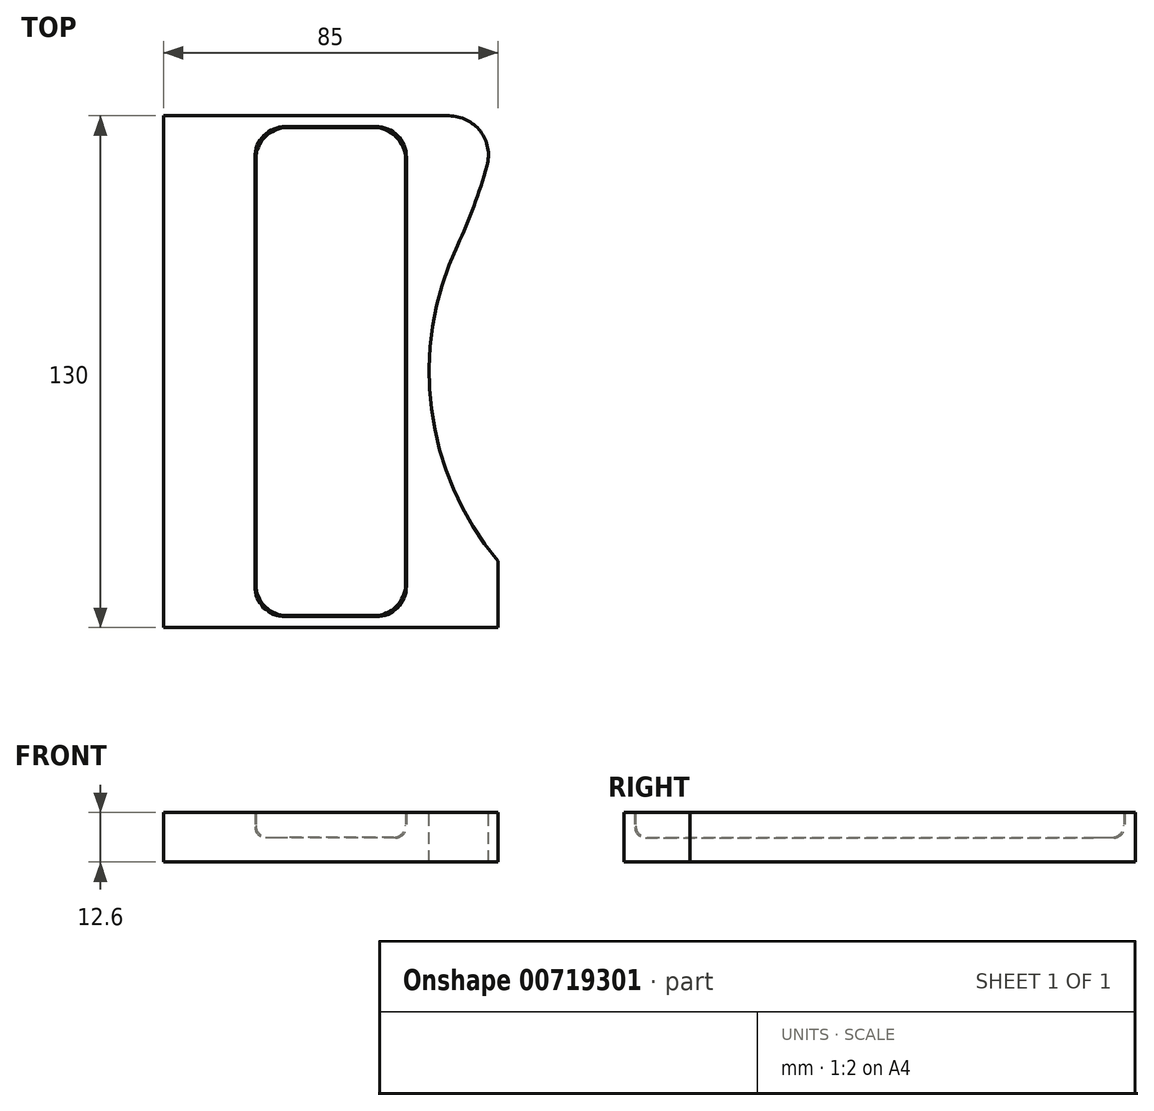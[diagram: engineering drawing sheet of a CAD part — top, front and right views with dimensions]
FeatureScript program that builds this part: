
annotation { "Feature Type Name" : "Feature", "Feature Type Description" : "" }
export const myFeature = defineFeature(function(context is Context, id is Id, definition is map)
    precondition{}
    {
        {
            var Q0;
            Q0=qCreatedBy(makeId("Top.planeOp"),FACE);
            var sketch = newSketch(context, id + "F0", { "sketchPlane" : qUnion([Q0])});
            skLineSegment(sketch, "E0.bottom", {"start": v(19, -62) * mm, "end": v(-19, -62) * mm});
            skLineSegment(sketch, "E0.top", {"start": v(19, 62) * mm, "end": v(-19, 62) * mm});
            skLineSegment(sketch, "E0.left", {"start": v(19, -62) * mm, "end": v(19, 62) * mm});
            skLineSegment(sketch, "E0.right", {"start": v(-19, -62) * mm, "end": v(-19, 62) * mm});
            skPoint(sketch, "E0.middle", {"position": v(0, 0) * mm});
            skSolve(sketch);
        }
        {
            var Q0;
            Q0=makeQuery(id+"F0.imprint","IMPRINT",FACE,{"disambiguationData":[TD([[makeQuery(id+"F0.imprint","IMPRINT",EDGE,{"derivedFrom":sQuery(id+"F0.wireOp",EDGE,"E0.bottom")}),-1.0]])]});
            extrude(context, id + "F1", {"entities" : qUnion([Q0]), "depth" : 6.3 * mm, "offsetDistance" : 25 * mm});
        }
        {
            var Q0;
            Q0=makeQuery(id+"F1.opExtrude","SWEPT_EDGE",EDGE,{"disambiguationData":[OSD([sQuery(id+"F0.wireOp",EDGE,"E0.top"),sQuery(id+"F0.wireOp",EDGE,"E0.left")])]});
            var Q1;
            Q1=makeQuery(id+"F1.opExtrude","SWEPT_EDGE",EDGE,{"disambiguationData":[OSD([sQuery(id+"F0.wireOp",EDGE,"E0.top"),sQuery(id+"F0.wireOp",EDGE,"E0.right")])]});
            var Q2;
            Q2=makeQuery(id+"F1.opExtrude","SWEPT_EDGE",EDGE,{"disambiguationData":[OSD([sQuery(id+"F0.wireOp",EDGE,"E0.bottom"),sQuery(id+"F0.wireOp",EDGE,"E0.left")])]});
            var Q3;
            Q3=makeQuery(id+"F1.opExtrude","SWEPT_EDGE",EDGE,{"disambiguationData":[OSD([sQuery(id+"F0.wireOp",EDGE,"E0.bottom"),sQuery(id+"F0.wireOp",EDGE,"E0.right")])]});
            fillet(context, id + "F2", {"entities" : qUnion([Q0, Q1, Q2, Q3]), "radius" : 8 * mm, "tangentPropagation" : true, "allowEdgeOverflow" : false});
        }
        {
            var Q0;
            Q0=makeQuery(id+"F1.opExtrude","CAP_FACE",FACE,{"disambiguationData":[OSD([sQuery(id+"F0.wireOp",EDGE,"E0.bottom"),sQuery(id+"F0.wireOp",EDGE,"E0.top"),sQuery(id+"F0.wireOp",EDGE,"E0.left"),sQuery(id+"F0.wireOp",EDGE,"E0.right")])],"isStart":true});
            fillet(context, id + "F3", {"entities" : qUnion([Q0]), "radius" : 3 * mm, "tangentPropagation" : true, "allowEdgeOverflow" : false});
        }
        {
            var Q0;
            Q0=qCreatedBy(makeId("Top.planeOp"),FACE);
            var sketch = newSketch(context, id + "F4", { "sketchPlane" : qUnion([Q0])});
            skLineSegment(sketch, "E1.bottom", {"start": v(19.25, -62.25) * mm, "end": v(-19.25, -62.25) * mm});
            skLineSegment(sketch, "E1.top", {"start": v(19.25, 62.25) * mm, "end": v(-19.25, 62.25) * mm});
            skLineSegment(sketch, "E1.left", {"start": v(19.25, -62.25) * mm, "end": v(19.25, 62.25) * mm});
            skLineSegment(sketch, "E1.right", {"start": v(-19.25, -62.25) * mm, "end": v(-19.25, 62.25) * mm});
            skPoint(sketch, "E1.middle", {"position": v(0, 0) * mm});
            skLineSegment(sketch, "E2.bottom", {"start": v(42.5, -65) * mm, "end": v(-42.5, -65) * mm});
            skLineSegment(sketch, "E2.top", {"start": v(42.5, 65) * mm, "end": v(-42.5, 65) * mm});
            skLineSegment(sketch, "E2.left", {"start": v(42.5, -65) * mm, "end": v(42.5, 65) * mm});
            skLineSegment(sketch, "E2.right", {"start": v(-42.5, -65) * mm, "end": v(-42.5, 65) * mm});
            skCircle(sketch, "E3", {"center": v(0, 65) * mm, "radius": 42.5 * mm});
            skCircle(sketch, "E4", {"center": v(0, -65) * mm, "radius": 42.5 * mm});
            skSolve(sketch);
        }
        {
            var Q0;
            Q0=makeQuery(id+"F4.imprint","IMPRINT",FACE,{"disambiguationData":[TD([[makeQuery(id+"F4.imprint","IMPRINT",EDGE,{"derivedFrom":sQuery(id+"F4.wireOp",EDGE,"E1.bottom")}),1.0]])]});
            var Q1;
            {var subQ5=sQuery(id+"F4.wireOp",EDGE,"E2.right");Q1=makeQuery(id+"F4.imprint","IMPRINT",FACE,{"disambiguationData":[TD([[makeQuery(id+"F4.imprint","IMPRINT",EDGE,{"derivedFrom":subQ5}),-1.0]])]});}
            var Q2;
            {var subQ5=sQuery(id+"F4.wireOp",EDGE,"E2.left");Q2=makeQuery(id+"F4.imprint","IMPRINT",FACE,{"disambiguationData":[TD([[makeQuery(id+"F4.imprint","IMPRINT",EDGE,{"derivedFrom":subQ5}),1.0]])]});}
            var Q3;
            {var subQ1=sQuery(id+"F4.wireOp",EDGE,"E1.top");Q3=makeQuery(id+"F4.imprint","IMPRINT",FACE,{"disambiguationData":[TD([[makeQuery(id+"F4.imprint","IMPRINT",EDGE,{"derivedFrom":subQ1}),-1.0]])]});}
            extrude(context, id + "F5", {"entities" : qUnion([Q0, Q1, Q2, Q3]), "endBound" : BoundingType.SYMMETRIC, "depth" : 12.6 * mm, "offsetDistance" : 25 * mm});
        }
        {
            var Q0;
            Q0=makeQuery(id+"F5.opExtrude","CAP_FACE",FACE,{"disambiguationData":[OSD([sQuery(id+"F4.wireOp",EDGE,"E1.bottom"),sQuery(id+"F4.wireOp",EDGE,"E1.top"),sQuery(id+"F4.wireOp",EDGE,"E1.left"),sQuery(id+"F4.wireOp",EDGE,"E1.right"),sQuery(id+"F4.wireOp",EDGE,"E2.bottom"),sQuery(id+"F4.wireOp",EDGE,"E2.top"),sQuery(id+"F4.wireOp",EDGE,"E2.left"),sQuery(id+"F4.wireOp",EDGE,"E2.right")])],"isStart":true});
            var sketch = newSketch(context, id + "F6", { "sketchPlane" : qUnion([Q0])});
            skLineSegment(sketch, "E5.bottom", {"start": v(19.25, -62.25) * mm, "end": v(-19.25, -62.25) * mm});
            skLineSegment(sketch, "E5.top", {"start": v(19.25, 62.25) * mm, "end": v(-19.25, 62.25) * mm});
            skLineSegment(sketch, "E5.left", {"start": v(19.25, -62.25) * mm, "end": v(19.25, 62.25) * mm});
            skLineSegment(sketch, "E5.right", {"start": v(-19.25, -62.25) * mm, "end": v(-19.25, 62.25) * mm});
            skPoint(sketch, "E5.middle", {"position": v(0, 0) * mm});
            skSolve(sketch);
        }
        {
            var Q0;
            Q0=makeQuery(id+"F6.imprint","IMPRINT",FACE,{"disambiguationData":[TD([[makeQuery(id+"F6.imprint","IMPRINT",EDGE,{"derivedFrom":sQuery(id+"F6.wireOp",EDGE,"E5.bottom")}),-1.0]])]});
            extrude(context, id + "F7", {"entities" : qUnion([Q0]), "operationType" : NewBodyOperationType.ADD, "oppositeDirection" : true, "depth" : 6.15 * mm, "offsetDistance" : 25 * mm});
        }
        {
            var Q0;
            Q0=makeQuery(id+"F5.opExtrude","SWEPT_EDGE",EDGE,{"disambiguationData":[OSD([sQuery(id+"F4.wireOp",EDGE,"E1.bottom"),sQuery(id+"F4.wireOp",EDGE,"E1.left")])]});
            var Q1;
            Q1=makeQuery(id+"F5.opExtrude","SWEPT_EDGE",EDGE,{"disambiguationData":[OSD([sQuery(id+"F4.wireOp",EDGE,"E1.bottom"),sQuery(id+"F4.wireOp",EDGE,"E1.right")])]});
            var Q2;
            Q2=makeQuery(id+"F5.opExtrude","SWEPT_EDGE",EDGE,{"disambiguationData":[OSD([sQuery(id+"F4.wireOp",EDGE,"E1.top"),sQuery(id+"F4.wireOp",EDGE,"E1.left")])]});
            var Q3;
            Q3=makeQuery(id+"F5.opExtrude","SWEPT_EDGE",EDGE,{"disambiguationData":[OSD([sQuery(id+"F4.wireOp",EDGE,"E1.top"),sQuery(id+"F4.wireOp",EDGE,"E1.right")])]});
            fillet(context, id + "F8", {"entities" : qUnion([Q0, Q1, Q2, Q3]), "radius" : 7.75 * mm, "tangentPropagation" : true, "allowEdgeOverflow" : false});
        }
        {
            var Q0;
            Q0=makeQuery(id+"F7.opExtrude","CAP_FACE",FACE,{"disambiguationData":[OSD([sQuery(id+"F6.wireOp",EDGE,"E5.bottom"),sQuery(id+"F6.wireOp",EDGE,"E5.top"),sQuery(id+"F6.wireOp",EDGE,"E5.left"),sQuery(id+"F6.wireOp",EDGE,"E5.right")])],"isStart":false});
            fillet(context, id + "F9", {"entities" : qUnion([Q0]), "radius" : 2.75 * mm, "tangentPropagation" : true, "allowEdgeOverflow" : false});
        }
        {
            var Q0;
            Q0=makeQuery(id+"F5.opExtrude","CAP_FACE",FACE,{"disambiguationData":[OSD([sQuery(id+"F4.wireOp",EDGE,"E1.bottom"),sQuery(id+"F4.wireOp",EDGE,"E1.top"),sQuery(id+"F4.wireOp",EDGE,"E1.left"),sQuery(id+"F4.wireOp",EDGE,"E1.right"),sQuery(id+"F4.wireOp",EDGE,"E2.bottom"),sQuery(id+"F4.wireOp",EDGE,"E2.top"),sQuery(id+"F4.wireOp",EDGE,"E2.left"),sQuery(id+"F4.wireOp",EDGE,"E2.right")])],"isStart":false});
            var sketch = newSketch(context, id + "F10", { "sketchPlane" : qUnion([Q0])});
            skLineSegment(sketch, "E6", {"start": v(-75.4, 0) * mm, "end": v(78.09, 0) * mm, "construction": true});
            skPoint(sketch, "E6.startSnap0", {"position": v(-42.5, 0) * mm});
            skPoint(sketch, "E7.endSnap0", {"position": v(0, -92.5) * mm});
            skLineSegment(sketch, "E8", {"start": v(0, -120.38) * mm, "end": v(0, 105.72) * mm, "construction": true});
            skCircle(sketch, "E9", {"center": v(100, 0) * mm, "radius": 75 * mm});
            skPoint(sketch, "E10", {"position": v(0, 0) * mm});
            skCircle(sketch, "E11.MirrorC", {"center": v(-100, 0) * mm, "radius": 75 * mm});
            skSolve(sketch);
        }
        {
            var Q0;
            {var subQ0=sQuery(id+"F10.wireOp",EDGE,"E11.MirrorC");var subQ1=makeQuery(id+"F5.opExtrude","CAP_EDGE",EDGE,{"disambiguationData":[OSD([sQuery(id+"F4.wireOp",EDGE,"E2.right")])],"isStart":false});var subQ2=makeQuery(id+"F10.imprint","INTERSECT",VERTEX,{"disambiguationData":[OD(0.0)],"derivedFrom":[subQ1,subQ0]});Q0=makeQuery(id+"F10.imprint","IMPRINT",FACE,{"disambiguationData":[TD([[makeQuery(id+"F10.imprint","IMPRINT",EDGE,{"disambiguationData":[TD([[subQ2,1.0]])],"derivedFrom":subQ0}),-1.0]])]});}
            var Q1;
            {var subQ0=sQuery(id+"F10.wireOp",EDGE,"E9");var subQ1=makeQuery(id+"F5.opExtrude","CAP_EDGE",EDGE,{"disambiguationData":[OSD([sQuery(id+"F4.wireOp",EDGE,"E2.left")])],"isStart":false});var subQ2=makeQuery(id+"F10.imprint","INTERSECT",VERTEX,{"disambiguationData":[OD(0.0)],"derivedFrom":[subQ1,subQ0]});Q1=makeQuery(id+"F10.imprint","IMPRINT",FACE,{"disambiguationData":[TD([[makeQuery(id+"F10.imprint","IMPRINT",EDGE,{"disambiguationData":[TD([[subQ2,1.0]])],"derivedFrom":subQ0}),1.0]])]});}
            extrude(context, id + "F11", {"entities" : qUnion([Q0, Q1]), "operationType" : NewBodyOperationType.REMOVE, "endBound" : BoundingType.THROUGH_ALL, "oppositeDirection" : true, "depth" : 25 * mm, "offsetDistance" : 25 * mm});
        }
        {
            var Q0;
            {var subQ0=sQuery(id+"F10.wireOp",EDGE,"E9");var subQ1=sQuery(id+"F4.wireOp",EDGE,"E2.left");Q0=makeQuery(id+"F11.boolean.opBoolean","COPY",EDGE,{"derivedFrom":makeQuery(id+"F11.opExtrude","SWEPT_EDGE",EDGE,{"disambiguationData":[OSD([subQ1,subQ0]),TDD([makeQuery(id+"F10.imprint","INTERSECT",VERTEX,{"disambiguationData":[OD(0.0)],"derivedFrom":[makeQuery(id+"F5.opExtrude","CAP_EDGE",EDGE,{"disambiguationData":[OSD([subQ1])],"isStart":false}),subQ0]})])]})});}
            var Q1;
            {var subQ0=sQuery(id+"F10.wireOp",EDGE,"E9");var subQ1=sQuery(id+"F4.wireOp",EDGE,"E2.left");Q1=makeQuery(id+"F11.boolean.opBoolean","COPY",EDGE,{"derivedFrom":makeQuery(id+"F11.opExtrude","SWEPT_EDGE",EDGE,{"disambiguationData":[OSD([subQ1,subQ0]),TDD([makeQuery(id+"F10.imprint","INTERSECT",VERTEX,{"disambiguationData":[OD(1.0)],"derivedFrom":[makeQuery(id+"F5.opExtrude","CAP_EDGE",EDGE,{"disambiguationData":[OSD([subQ1])],"isStart":false}),subQ0]})])]})});}
            var Q2;
            {var subQ0=sQuery(id+"F10.wireOp",EDGE,"E11.MirrorC");var subQ1=sQuery(id+"F4.wireOp",EDGE,"E2.right");Q2=makeQuery(id+"F11.boolean.opBoolean","COPY",EDGE,{"derivedFrom":makeQuery(id+"F11.opExtrude","SWEPT_EDGE",EDGE,{"disambiguationData":[OSD([subQ1,subQ0]),TDD([makeQuery(id+"F10.imprint","INTERSECT",VERTEX,{"disambiguationData":[OD(0.0)],"derivedFrom":[makeQuery(id+"F5.opExtrude","CAP_EDGE",EDGE,{"disambiguationData":[OSD([subQ1])],"isStart":false}),subQ0]})])]})});}
            var Q3;
            {var subQ0=sQuery(id+"F10.wireOp",EDGE,"E11.MirrorC");var subQ1=sQuery(id+"F4.wireOp",EDGE,"E2.right");Q3=makeQuery(id+"F11.boolean.opBoolean","COPY",EDGE,{"derivedFrom":makeQuery(id+"F11.opExtrude","SWEPT_EDGE",EDGE,{"disambiguationData":[OSD([subQ1,subQ0]),TDD([makeQuery(id+"F10.imprint","INTERSECT",VERTEX,{"disambiguationData":[OD(1.0)],"derivedFrom":[makeQuery(id+"F5.opExtrude","CAP_EDGE",EDGE,{"disambiguationData":[OSD([subQ1])],"isStart":false}),subQ0]})])]})});}
            fillet(context, id + "F12", {"entities" : qUnion([Q0, Q1, Q2, Q3]), "radius" : 125 * mm, "tangentPropagation" : true, "allowEdgeOverflow" : false});
        }
        {
            var Q0;
            {var subQ0=sQuery(id+"F10.wireOp",EDGE,"E11.MirrorC");var subQ1=sQuery(id+"F4.wireOp",EDGE,"E2.right");Q0=makeQuery(id+"F12.opFillet","BLEND_EDGE",EDGE,{"blendedFrom":[makeQuery(id+"F11.boolean.opBoolean","COPY",EDGE,{"derivedFrom":makeQuery(id+"F11.opExtrude","SWEPT_EDGE",EDGE,{"disambiguationData":[OSD([subQ1,subQ0]),TDD([makeQuery(id+"F10.imprint","INTERSECT",VERTEX,{"disambiguationData":[OD(1.0)],"derivedFrom":[makeQuery(id+"F5.opExtrude","CAP_EDGE",EDGE,{"disambiguationData":[OSD([subQ1])],"isStart":false}),subQ0]})])]})}),makeQuery(id+"F5.opExtrude","SWEPT_FACE",FACE,{"disambiguationData":[OSD([sQuery(id+"F4.wireOp",EDGE,"E2.top")])]})],"blendedInto":[makeQuery(id+"F5.opExtrude","SWEPT_FACE",FACE,{"disambiguationData":[OSD([sQuery(id+"F4.wireOp",EDGE,"E2.top")])]})]});}
            var Q1;
            {var subQ0=sQuery(id+"F10.wireOp",EDGE,"E9");var subQ1=sQuery(id+"F4.wireOp",EDGE,"E2.left");Q1=makeQuery(id+"F12.opFillet","BLEND_EDGE",EDGE,{"blendedFrom":[makeQuery(id+"F11.boolean.opBoolean","COPY",EDGE,{"derivedFrom":makeQuery(id+"F11.opExtrude","SWEPT_EDGE",EDGE,{"disambiguationData":[OSD([subQ1,subQ0]),TDD([makeQuery(id+"F10.imprint","INTERSECT",VERTEX,{"disambiguationData":[OD(1.0)],"derivedFrom":[makeQuery(id+"F5.opExtrude","CAP_EDGE",EDGE,{"disambiguationData":[OSD([subQ1])],"isStart":false}),subQ0]})])]})}),makeQuery(id+"F5.opExtrude","SWEPT_FACE",FACE,{"disambiguationData":[OSD([sQuery(id+"F4.wireOp",EDGE,"E2.top")])]})],"blendedInto":[makeQuery(id+"F5.opExtrude","SWEPT_FACE",FACE,{"disambiguationData":[OSD([sQuery(id+"F4.wireOp",EDGE,"E2.top")])]})]});}
            var Q2;
            {var subQ0=sQuery(id+"F10.wireOp",EDGE,"E11.MirrorC");var subQ1=sQuery(id+"F4.wireOp",EDGE,"E2.right");Q2=makeQuery(id+"F12.opFillet","BLEND_EDGE",EDGE,{"blendedFrom":[makeQuery(id+"F11.boolean.opBoolean","COPY",EDGE,{"derivedFrom":makeQuery(id+"F11.opExtrude","SWEPT_EDGE",EDGE,{"disambiguationData":[OSD([subQ1,subQ0]),TDD([makeQuery(id+"F10.imprint","INTERSECT",VERTEX,{"disambiguationData":[OD(0.0)],"derivedFrom":[makeQuery(id+"F5.opExtrude","CAP_EDGE",EDGE,{"disambiguationData":[OSD([subQ1])],"isStart":false}),subQ0]})])]})}),makeQuery(id+"F5.opExtrude","SWEPT_FACE",FACE,{"disambiguationData":[OSD([sQuery(id+"F4.wireOp",EDGE,"E2.bottom")])]})],"blendedInto":[makeQuery(id+"F5.opExtrude","SWEPT_FACE",FACE,{"disambiguationData":[OSD([sQuery(id+"F4.wireOp",EDGE,"E2.bottom")])]})]});}
            var Q3;
            {var subQ0=sQuery(id+"F10.wireOp",EDGE,"E9");var subQ1=sQuery(id+"F4.wireOp",EDGE,"E2.left");Q3=makeQuery(id+"F12.opFillet","BLEND_EDGE",EDGE,{"blendedFrom":[makeQuery(id+"F11.boolean.opBoolean","COPY",EDGE,{"derivedFrom":makeQuery(id+"F11.opExtrude","SWEPT_EDGE",EDGE,{"disambiguationData":[OSD([subQ1,subQ0]),TDD([makeQuery(id+"F10.imprint","INTERSECT",VERTEX,{"disambiguationData":[OD(0.0)],"derivedFrom":[makeQuery(id+"F5.opExtrude","CAP_EDGE",EDGE,{"disambiguationData":[OSD([subQ1])],"isStart":false}),subQ0]})])]})}),makeQuery(id+"F5.opExtrude","SWEPT_FACE",FACE,{"disambiguationData":[OSD([sQuery(id+"F4.wireOp",EDGE,"E2.bottom")])]})],"blendedInto":[makeQuery(id+"F5.opExtrude","SWEPT_FACE",FACE,{"disambiguationData":[OSD([sQuery(id+"F4.wireOp",EDGE,"E2.bottom")])]})]});}
            fillet(context, id + "F13", {"entities" : qUnion([Q0, Q1, Q2, Q3]), "radius" : 10 * mm, "tangentPropagation" : true, "allowEdgeOverflow" : false});
        }
    });
